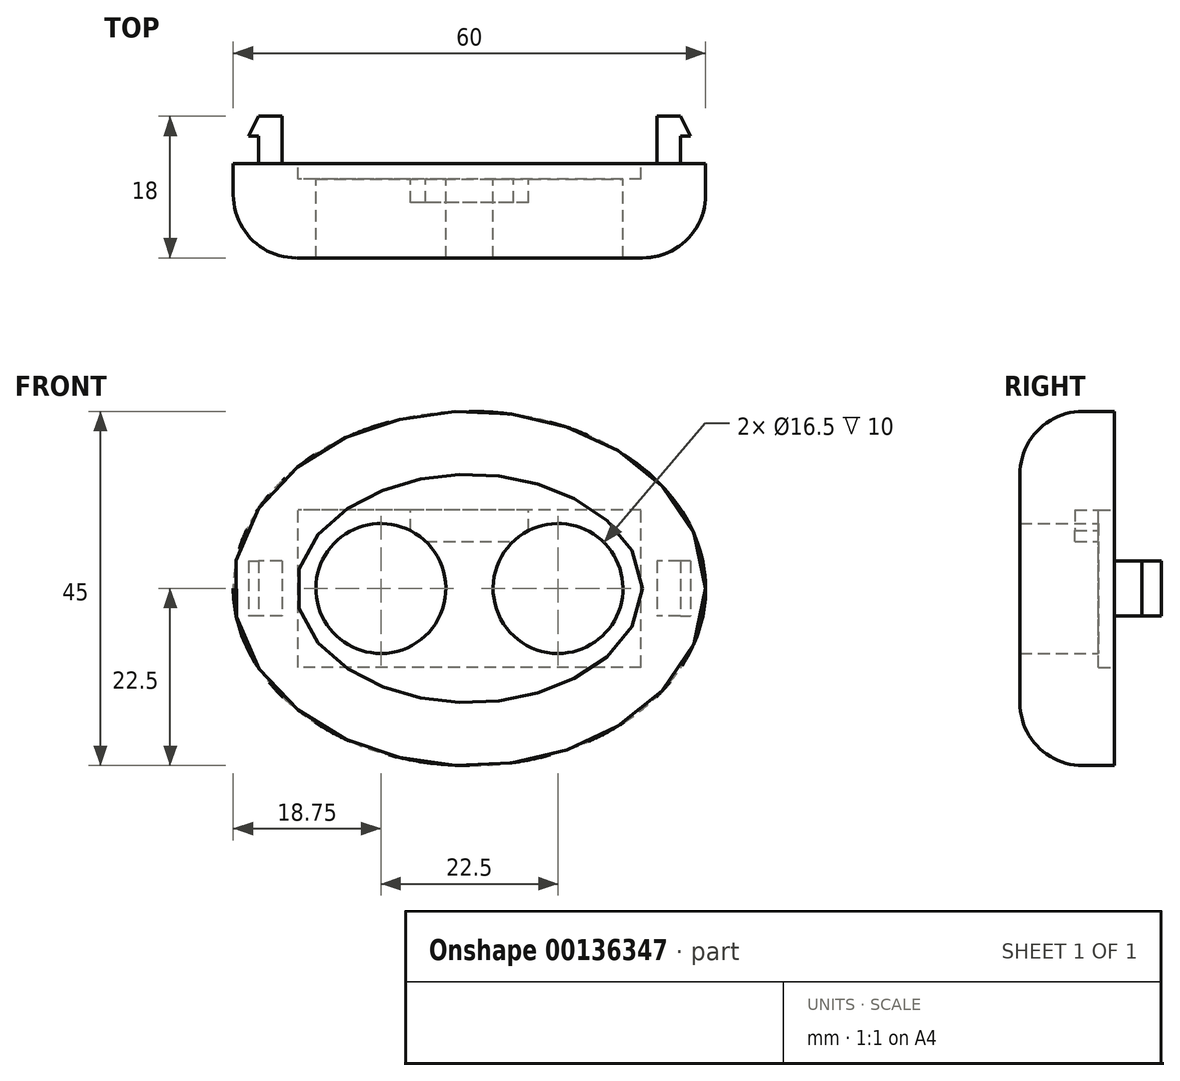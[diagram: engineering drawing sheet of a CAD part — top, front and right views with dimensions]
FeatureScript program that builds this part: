
annotation { "Feature Type Name" : "Feature", "Feature Type Description" : "" }
export const myFeature = defineFeature(function(context is Context, id is Id, definition is map)
    precondition{}
    {
        {
            var Q0;
            Q0=qCreatedBy(makeId("Front.planeOp"),FACE);
            var sketch = newSketch(context, id + "F0", { "sketchPlane" : qUnion([Q0])});
            skCircle(sketch, "E0", {"center": v(-11.25, 0) * mm, "radius": 8.25 * mm});
            skCircle(sketch, "E1", {"center": v(11.25, 0) * mm, "radius": 8.25 * mm});
            skLineSegment(sketch, "E2", {"start": v(-11.25, 0) * mm, "end": v(11.25, 0) * mm, "construction": true});
            skEllipse(sketch, "E3", {"center": v(0, 0) * mm, "majorRadius": 30 * mm, "minorRadius": 22.5 * mm, "majorAxis": v(1, 0)});
            skLineSegment(sketch, "E4.bottom", {"start": v(21.8, -10) * mm, "end": v(-21.8, -10) * mm});
            skLineSegment(sketch, "E4.top", {"start": v(21.8, 10) * mm, "end": v(7.5, 10) * mm});
            skLineSegment(sketch, "E4.left", {"start": v(21.8, -10) * mm, "end": v(21.8, 10) * mm});
            skLineSegment(sketch, "E4.right", {"start": v(-21.8, -10) * mm, "end": v(-21.8, 10) * mm});
            skLineSegment(sketch, "E5", {"start": v(5.59, 10) * mm, "end": v(5.59, 6) * mm, "construction": true});
            skLineSegment(sketch, "E6", {"start": v(-5.59, 6) * mm, "end": v(-5.59, 10) * mm, "construction": true});
            skLineSegment(sketch, "E7", {"start": v(7.5, 10) * mm, "end": v(7.5, 7.35) * mm});
            skLineSegment(sketch, "E8", {"start": v(-7.5, 10) * mm, "end": v(-7.5, 7.35) * mm});
            skLineSegment(sketch, "E9", {"start": v(5.59, 6) * mm, "end": v(-5.59, 6) * mm});
            skLineSegment(sketch, "E10", {"start": v(7.5, 7.35) * mm, "end": v(-7.5, 7.35) * mm, "construction": true});
            skLineSegment(sketch, "E11", {"start": v(7.5, 10) * mm, "end": v(-7.5, 10) * mm});
            skLineSegment(sketch, "E12", {"start": v(-7.5, 10) * mm, "end": v(-21.8, 10) * mm});
            skLineSegment(sketch, "E13.top", {"start": v(7.5, 18) * mm, "end": v(-7.5, 18) * mm, "construction": true});
            skLineSegment(sketch, "E13.left", {"start": v(7.5, 10) * mm, "end": v(7.5, 18) * mm, "construction": true});
            skLineSegment(sketch, "E13.right", {"start": v(-7.5, 10) * mm, "end": v(-7.5, 18) * mm, "construction": true});
            skLineSegment(sketch, "E14", {"start": v(0, 18) * mm, "end": v(0, 10) * mm, "construction": true});
            skSolve(sketch);
        }
        {
            var Q0;
            Q0=makeQuery(id+"F0.imprint","IMPRINT",FACE,{"disambiguationData":[TD([[makeQuery(id+"F0.imprint","IMPRINT",EDGE,{"derivedFrom":sQuery(id+"F0.wireOp",EDGE,"E3")}),1.0]])]});
            var Q1;
            Q1=makeQuery(id+"F0.imprint","IMPRINT",FACE,{"disambiguationData":[TD([[makeQuery(id+"F0.imprint","IMPRINT",EDGE,{"derivedFrom":sQuery(id+"F0.wireOp",EDGE,"E4.bottom")}),-1.0]])]});
            var Q2;
            {var subQ1=sQuery(id+"F0.wireOp",EDGE,"E7");Q2=makeQuery(id+"F0.imprint","IMPRINT",FACE,{"disambiguationData":[TD([[makeQuery(id+"F0.imprint","IMPRINT",EDGE,{"derivedFrom":subQ1}),-1.0]])]});}
            extrude(context, id + "F1", {"entities" : qUnion([Q0, Q1, Q2]), "depth" : 12 * mm});
        }
        {
            var Q0;
            Q0=makeQuery(id+"F0.imprint","IMPRINT",FACE,{"disambiguationData":[TD([[makeQuery(id+"F0.imprint","IMPRINT",EDGE,{"derivedFrom":sQuery(id+"F0.wireOp",EDGE,"E4.bottom")}),-1.0]])]});
            var Q1;
            {var subQ1=sQuery(id+"F0.wireOp",EDGE,"E7");Q1=makeQuery(id+"F0.imprint","IMPRINT",FACE,{"disambiguationData":[TD([[makeQuery(id+"F0.imprint","IMPRINT",EDGE,{"derivedFrom":subQ1}),-1.0]])]});}
            extrude(context, id + "F2", {"entities" : qUnion([Q0, Q1]), "operationType" : NewBodyOperationType.REMOVE, "depth" : 2 * mm});
        }
        {
            var Q0;
            Q0=makeQuery(id+"F1.opExtrude","CAP_EDGE",EDGE,{"disambiguationData":[OSD([sQuery(id+"F0.wireOp",EDGE,"E3")])],"isStart":false});
            fillet(context, id + "F3", {"entities" : qUnion([Q0]), "radius" : 8 * mm, "tangentPropagation" : true, "allowEdgeOverflow" : false});
        }
        {
            var Q0;
            {var subQ1=sQuery(id+"F0.wireOp",EDGE,"E7");Q0=makeQuery(id+"F0.imprint","IMPRINT",FACE,{"disambiguationData":[TD([[makeQuery(id+"F0.imprint","IMPRINT",EDGE,{"derivedFrom":subQ1}),-1.0]])]});}
            extrude(context, id + "F4", {"entities" : qUnion([Q0]), "operationType" : NewBodyOperationType.REMOVE, "depth" : 5 * mm});
        }
        {
            var Q0;
            Q0=makeQuery(id+"F0.imprint","IMPRINT",FACE,{"disambiguationData":[TD([[makeQuery(id+"F0.imprint","IMPRINT",EDGE,{"derivedFrom":sQuery(id+"F0.wireOp",EDGE,"E3")}),1.0]])]});
            var sketch = newSketch(context, id + "F5", { "sketchPlane" : qUnion([Q0])});
            skLineSegment(sketch, "E15.bottom", {"start": v(26.8, 3.5) * mm, "end": v(23.8, 3.5) * mm});
            skLineSegment(sketch, "E15.top", {"start": v(26.8, -3.5) * mm, "end": v(23.8, -3.5) * mm});
            skLineSegment(sketch, "E15.left", {"start": v(26.8, 3.5) * mm, "end": v(26.8, -3.5) * mm});
            skLineSegment(sketch, "E15.right", {"start": v(23.8, 3.5) * mm, "end": v(23.8, -3.5) * mm});
            skLineSegment(sketch, "E16.bottom", {"start": v(-23.8, 3.5) * mm, "end": v(-26.8, 3.5) * mm});
            skLineSegment(sketch, "E16.top", {"start": v(-23.8, -3.5) * mm, "end": v(-26.8, -3.5) * mm});
            skLineSegment(sketch, "E16.left", {"start": v(-23.8, 3.5) * mm, "end": v(-23.8, -3.5) * mm});
            skLineSegment(sketch, "E16.right", {"start": v(-26.8, 3.5) * mm, "end": v(-26.8, -3.5) * mm});
            skLineSegment(sketch, "E17", {"start": v(23.8, 3.5) * mm, "end": v(-23.8, 3.5) * mm, "construction": true});
            skLineSegment(sketch, "E18", {"start": v(23.8, 0) * mm, "end": v(21.8, 0) * mm, "construction": true});
            skLineSegment(sketch, "E19", {"start": v(23.8, -3.5) * mm, "end": v(-23.8, -3.5) * mm});
            skSolve(sketch);
        }
        {
            var Q0;
            Q0 = qSketchRegion(id + "F5", true);
            extrude(context, id + "F6", {"entities" : qUnion([Q0]), "operationType" : NewBodyOperationType.ADD, "oppositeDirection" : true, "depth" : 6 * mm});
        }
        {
            var Q0;
            Q0=makeQuery(id+"F6.opExtrude","SWEPT_FACE",FACE,{"disambiguationData":[OSD([sQuery(id+"F5.wireOp",EDGE,"E15.top")])]});
            var sketch = newSketch(context, id + "F7", { "sketchPlane" : qUnion([Q0])});
            skLineSegment(sketch, "E20", {"start": v(26.8, -6) * mm, "end": v(28.05, -3.5) * mm});
            skLineSegment(sketch, "E21", {"start": v(28.05, -3.5) * mm, "end": v(26.8, -3.5) * mm});
            skLineSegment(sketch, "E22", {"start": v(26.8, -3.5) * mm, "end": v(26.8, -6) * mm});
            skLineSegment(sketch, "E23", {"start": v(-26.8, -6) * mm, "end": v(-26.8, -3.5) * mm});
            skLineSegment(sketch, "E24", {"start": v(-26.8, -3.5) * mm, "end": v(-28.05, -3.5) * mm});
            skLineSegment(sketch, "E25", {"start": v(-28.05, -3.5) * mm, "end": v(-26.8, -6) * mm});
            skSolve(sketch);
        }
        {
            var Q0;
            Q0 = qSketchRegion(id + "F7", true);
            var Q1;
            Q1=makeQuery(id+"F6.opExtrude","SWEPT_FACE",FACE,{"disambiguationData":[OSD([sQuery(id+"F5.wireOp",EDGE,"E15.bottom")])]});
            extrude(context, id + "F8", {"entities" : qUnion([Q0]), "operationType" : NewBodyOperationType.ADD, "endBound" : BoundingType.UP_TO_SURFACE, "oppositeDirection" : true, "endBoundEntityFace" : qUnion([Q1]), "depth" : 25 * mm});
        }
    });
